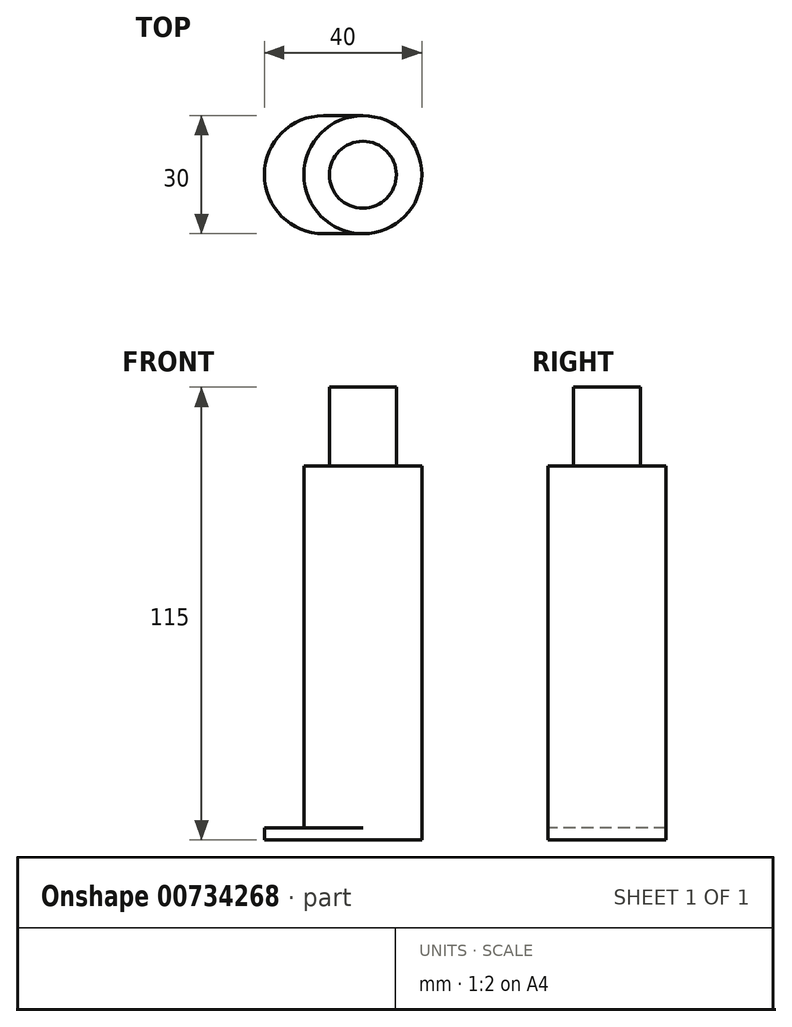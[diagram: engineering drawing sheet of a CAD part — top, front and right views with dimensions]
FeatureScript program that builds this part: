
annotation { "Feature Type Name" : "Feature", "Feature Type Description" : "" }
export const myFeature = defineFeature(function(context is Context, id is Id, definition is map)
    precondition{}
    {
        {
            var Q0;
            Q0=qCreatedBy(makeId("Top.planeOp"),FACE);
            var sketch = newSketch(context, id + "F0", { "sketchPlane" : qUnion([Q0])});
            skCircle(sketch, "E0", {"center": v(0, 0) * mm, "radius": 8.5 * mm});
            skCircle(sketch, "E1", {"center": v(0, 0) * mm, "radius": 15 * mm});
            skLineSegment(sketch, "E2", {"start": v(0, 0) * mm, "end": v(-10, 0) * mm});
            skArc(sketch, "E3", {"start": v(-10, 15) * mm, "mid": v(-25, 0) * mm, "end": v(-10, -15) * mm});
            skLineSegment(sketch, "E4", {"start": v(0, 15) * mm, "end": v(-10, 15) * mm});
            skLineSegment(sketch, "E5", {"start": v(0, -15) * mm, "end": v(-10, -15) * mm});
            skSolve(sketch);
        }
        {
            var Q0;
            Q0=makeQuery(id+"F0.imprint","IMPRINT",FACE,{"disambiguationData":[TD([[makeQuery(id+"F0.imprint","IMPRINT",EDGE,{"derivedFrom":sQuery(id+"F0.wireOp",EDGE,"E3")}),1.0]])]});
            var Q1;
            Q1=makeQuery(id+"F0.imprint","IMPRINT",FACE,{"disambiguationData":[TD([[makeQuery(id+"F0.imprint","IMPRINT",EDGE,{"derivedFrom":sQuery(id+"F0.wireOp",EDGE,"E0")}),-1.0]])]});
            var Q2;
            Q2=makeQuery(id+"F0.imprint","IMPRINT",FACE,{"disambiguationData":[TD([[makeQuery(id+"F0.imprint","IMPRINT",EDGE,{"derivedFrom":sQuery(id+"F0.wireOp",EDGE,"E0")}),1.0]])]});
            extrude(context, id + "F1", {"entities" : qUnion([Q0, Q1, Q2]), "depth" : 3 * mm, "offsetDistance" : 25 * mm});
        }
        {
            var Q0;
            Q0=makeQuery(id+"F0.imprint","IMPRINT",FACE,{"disambiguationData":[TD([[makeQuery(id+"F0.imprint","IMPRINT",EDGE,{"derivedFrom":sQuery(id+"F0.wireOp",EDGE,"E0")}),-1.0]])]});
            var Q1;
            Q1=makeQuery(id+"F0.imprint","IMPRINT",FACE,{"disambiguationData":[TD([[makeQuery(id+"F0.imprint","IMPRINT",EDGE,{"derivedFrom":sQuery(id+"F0.wireOp",EDGE,"E0")}),1.0]])]});
            extrude(context, id + "F2", {"entities" : qUnion([Q0, Q1]), "operationType" : NewBodyOperationType.ADD, "depth" : 95 * mm, "offsetDistance" : 25 * mm});
        }
        {
            var Q0;
            Q0=makeQuery(id+"F0.imprint","IMPRINT",FACE,{"disambiguationData":[TD([[makeQuery(id+"F0.imprint","IMPRINT",EDGE,{"derivedFrom":sQuery(id+"F0.wireOp",EDGE,"E0")}),1.0]])]});
            extrude(context, id + "F3", {"entities" : qUnion([Q0]), "operationType" : NewBodyOperationType.ADD, "depth" : 115 * mm, "offsetDistance" : 25 * mm});
        }
    });
